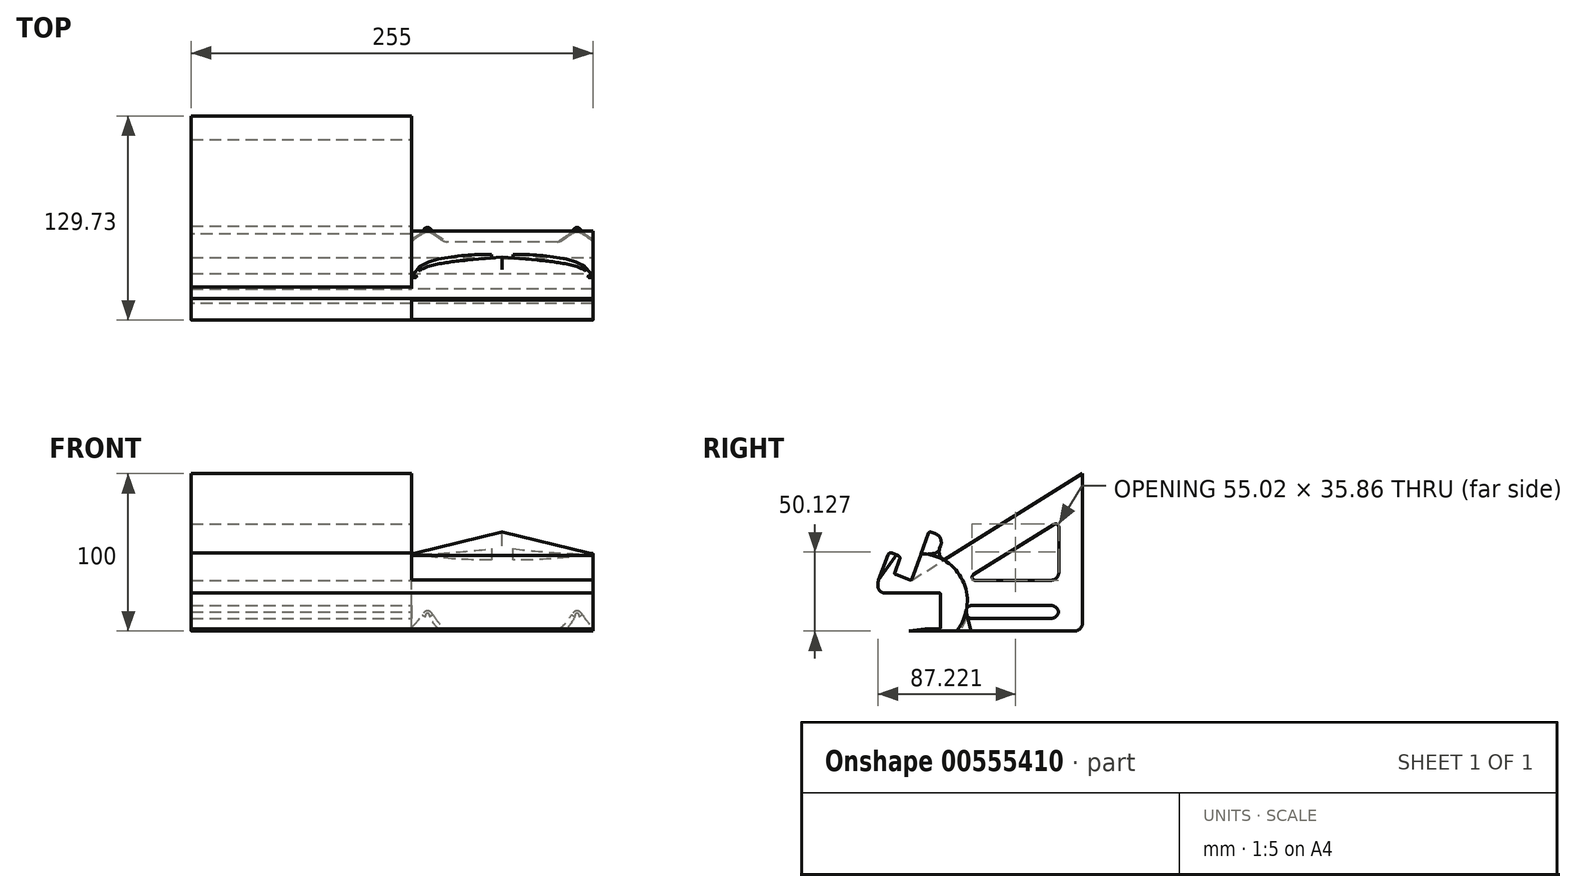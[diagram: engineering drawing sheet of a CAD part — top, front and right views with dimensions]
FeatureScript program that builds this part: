
annotation { "Feature Type Name" : "Feature", "Feature Type Description" : "" }
export const myFeature = defineFeature(function(context is Context, id is Id, definition is map)
    precondition{}
    {
        {
            var Q0;
            Q0=qCreatedBy(makeId("Right.planeOp"),FACE);
            var sketch = newSketch(context, id + "F0", { "sketchPlane" : qUnion([Q0])});
            skLineSegment(sketch, "E0", {"start": v(0, 0) * mm, "end": v(0, 100) * mm});
            skLineSegment(sketch, "E1", {"start": v(0, 0) * mm, "end": v(-110, 0) * mm});
            skLineSegment(sketch, "E2", {"start": v(-110, 0) * mm, "end": v(-110, 1.2) * mm});
            skLineSegment(sketch, "E3", {"start": v(-110, 1.2) * mm, "end": v(-90, 1.2) * mm});
            skLineSegment(sketch, "E4", {"start": v(-90, 1.2) * mm, "end": v(-90, 24.2) * mm});
            skLineSegment(sketch, "E5", {"start": v(-90, 24.2) * mm, "end": v(-110, 24.2) * mm});
            skLineSegment(sketch, "E6", {"start": v(-110, 24.2) * mm, "end": v(-129.73, 31.38) * mm});
            skLineSegment(sketch, "E7", {"start": v(-129.73, 31.38) * mm, "end": v(-122.9, 50.18) * mm});
            skLineSegment(sketch, "E8.0", {"start": v(-119.48, 36.16) * mm, "end": v(-115.38, 47.44) * mm});
            skLineSegment(sketch, "E8.1", {"start": v(-108.59, 32.2) * mm, "end": v(-119.48, 36.16) * mm});
            skLineSegment(sketch, "E9", {"start": v(-122.9, 50.18) * mm, "end": v(-115.38, 47.44) * mm});
            skLineSegment(sketch, "E10", {"start": v(-108.59, 32.2) * mm, "end": v(-108.59, 24.2) * mm, "construction": true});
            skLineSegment(sketch, "E11", {"start": v(-108.59, 32.2) * mm, "end": v(0, 100) * mm});
            skLineSegment(sketch, "E12", {"start": v(-129.73, 31.38) * mm, "end": v(-129.73, 24.2) * mm});
            skLineSegment(sketch, "E13", {"start": v(-129.73, 24.2) * mm, "end": v(-110, 24.2) * mm});
            skLineSegment(sketch, "E14", {"start": v(-75, 24.2) * mm, "end": v(-15, 24.2) * mm});
            skLineSegment(sketch, "E15", {"start": v(-75, 24.2) * mm, "end": v(-75, 32.2) * mm});
            skLineSegment(sketch, "E16", {"start": v(-75, 32.2) * mm, "end": v(-15, 69.66) * mm});
            skLineSegment(sketch, "E17", {"start": v(-15, 24.2) * mm, "end": v(-15, 69.66) * mm});
            skLineSegment(sketch, "E18", {"start": v(-75, 32.2) * mm, "end": v(-15, 32.2) * mm});
            skLineSegment(sketch, "E19", {"start": v(-15, 16.2) * mm, "end": v(-15, 8) * mm});
            skLineSegment(sketch, "E20", {"start": v(-15, 16.2) * mm, "end": v(-75, 16.2) * mm});
            skLineSegment(sketch, "E21", {"start": v(-75, 16.2) * mm, "end": v(-75, 8) * mm});
            skLineSegment(sketch, "E22", {"start": v(-75, 8) * mm, "end": v(-15, 8) * mm});
            skLineSegment(sketch, "E23", {"start": v(-90, 0) * mm, "end": v(-80, 0) * mm, "construction": true});
            skSolve(sketch);
        }
        {
            var Q0;
            Q0=makeQuery(id+"F0.imprint","IMPRINT",FACE,{"disambiguationData":[TD([[makeQuery(id+"F0.imprint","IMPRINT",EDGE,{"derivedFrom":sQuery(id+"F0.wireOp",EDGE,"E0")}),1.0]])]});
            var Q1;
            {var subQ0=sQuery(id+"F0.wireOp",EDGE,"E14");Q1=makeQuery(id+"F0.imprint","IMPRINT",FACE,{"disambiguationData":[TD([[makeQuery(id+"F0.imprint","IMPRINT",EDGE,{"derivedFrom":subQ0}),1.0]])]});}
            var Q2;
            Q2=makeQuery(id+"F0.imprint","IMPRINT",FACE,{"disambiguationData":[TD([[makeQuery(id+"F0.imprint","IMPRINT",EDGE,{"derivedFrom":sQuery(id+"F0.wireOp",EDGE,"E6")}),1.0]])]});
            extrude(context, id + "F1", {"entities" : qUnion([Q0, Q1, Q2]), "oppositeDirection" : true, "depth" : 140 * mm, "offsetDistance" : 25 * mm});
        }
        {
            var Q0;
            Q0=qCreatedBy(makeId("Right.planeOp"),FACE);
            var sketch = newSketch(context, id + "F2", { "sketchPlane" : qUnion([Q0])});
            skLineSegment(sketch, "E24.0", {"start": v(-122.9, 50.18) * mm, "end": v(-115.38, 47.44) * mm});
            skLineSegment(sketch, "E24.1", {"start": v(-129.73, 31.38) * mm, "end": v(-122.9, 50.18) * mm});
            skLineSegment(sketch, "E24.2", {"start": v(-119.48, 36.16) * mm, "end": v(-115.38, 47.44) * mm});
            skLineSegment(sketch, "E24.3", {"start": v(-108.59, 32.2) * mm, "end": v(-119.48, 36.16) * mm});
            skLineSegment(sketch, "E24.4", {"start": v(-110, 24.2) * mm, "end": v(-129.73, 31.38) * mm});
            skLineSegment(sketch, "E24.5", {"start": v(-129.73, 24.2) * mm, "end": v(-110, 24.2) * mm});
            skLineSegment(sketch, "E24.6", {"start": v(-129.73, 31.38) * mm, "end": v(-129.73, 24.2) * mm});
            skLineSegment(sketch, "E24.7", {"start": v(-90, 24.2) * mm, "end": v(-110, 24.2) * mm});
            skLineSegment(sketch, "E24.8", {"start": v(-90, 1.2) * mm, "end": v(-90, 24.2) * mm});
            skLineSegment(sketch, "E24.9", {"start": v(-110, 1.2) * mm, "end": v(-90, 1.2) * mm});
            skLineSegment(sketch, "E24.10", {"start": v(0, 0) * mm, "end": v(-110, 0) * mm});
            skLineSegment(sketch, "E24.11", {"start": v(-110, 0) * mm, "end": v(-110, 1.2) * mm});
            skLineSegment(sketch, "E25", {"start": v(-90, 0) * mm, "end": v(-80, 0) * mm, "construction": true});
            skArc(sketch, "E26", {"start": v(-80, 0) * mm, "mid": v(-85.1, 24.26) * mm, "end": v(-108.59, 32.2) * mm});
            skLineSegment(sketch, "E27", {"start": v(-108.59, 32.2) * mm, "end": v(-102.41, 49.17) * mm});
            skLineSegment(sketch, "E28", {"start": v(-108.59, 32.2) * mm, "end": v(-80, 0) * mm, "construction": true});
            skLineSegment(sketch, "E29", {"start": v(-94.3, 16.1) * mm, "end": v(-85.1, 24.26) * mm, "construction": true});
            skArc(sketch, "E30", {"start": v(-80, 0) * mm, "mid": v(-75.77, 31.62) * mm, "end": v(-102.41, 49.17) * mm});
            skLineSegment(sketch, "E31", {"start": v(-103.07, 19.18) * mm, "end": v(-90, 24.2) * mm, "construction": true});
            skLineSegment(sketch, "E32", {"start": v(-94.3, 16.1) * mm, "end": v(-76.08, 32.27) * mm, "construction": true});
            skSolve(sketch);
        }
        {
            var Q0;
            Q0=makeQuery(id+"F2.imprint","IMPRINT",FACE,{"disambiguationData":[TD([[makeQuery(id+"F2.imprint","IMPRINT",EDGE,{"derivedFrom":sQuery(id+"F2.wireOp",EDGE,"E24.4")}),1.0]])]});
            var Q1;
            Q1=makeQuery(id+"F2.imprint","IMPRINT",FACE,{"disambiguationData":[TD([[makeQuery(id+"F2.imprint","IMPRINT",EDGE,{"derivedFrom":sQuery(id+"F2.wireOp",EDGE,"E24.0")}),-1.0]])]});
            var Q2;
            Q2=makeQuery(id+"F2.imprint","IMPRINT",FACE,{"disambiguationData":[TD([[makeQuery(id+"F2.imprint","IMPRINT",EDGE,{"derivedFrom":sQuery(id+"F2.wireOp",EDGE,"E26")}),-1.0]])]});
            extrude(context, id + "F3", {"entities" : qUnion([Q0, Q1, Q2]), "depth" : 115 * mm, "offsetDistance" : 25 * mm});
        }
        {
            var Q0;
            Q0=makeQuery(id+"F1.opExtrude","SWEPT_EDGE",EDGE,{"disambiguationData":[OSD([sQuery(id+"F0.wireOp",EDGE,"E8.0"),sQuery(id+"F0.wireOp",EDGE,"E8.1")])]});
            var Q1;
            Q1=makeQuery(id+"F3.opExtrude","SWEPT_EDGE",EDGE,{"disambiguationData":[OSD([sQuery(id+"F2.wireOp",EDGE,"E24.2"),sQuery(id+"F2.wireOp",EDGE,"E24.3")])]});
            var Q2;
            Q2=makeQuery(id+"F3.opExtrude","SWEPT_EDGE",EDGE,{"disambiguationData":[OSD([sQuery(id+"F2.wireOp",EDGE,"E24.3"),sQuery(id+"F2.wireOp",EDGE,"E26"),sQuery(id+"F2.wireOp",EDGE,"E27")])]});
            fillet(context, id + "F4", {"entities" : qUnion([Q0, Q1, Q2]), "radius" : 1 * mm, "tangentPropagation" : true, "allowEdgeOverflow" : false});
        }
        {
            var Q0;
            Q0=makeQuery(id+"F1.opExtrude","SWEPT_EDGE",EDGE,{"disambiguationData":[OSD([sQuery(id+"F0.wireOp",EDGE,"E6"),sQuery(id+"F0.wireOp",EDGE,"E7"),sQuery(id+"F0.wireOp",EDGE,"E12")])]});
            var Q1;
            Q1=makeQuery(id+"F3.opExtrude","SWEPT_EDGE",EDGE,{"disambiguationData":[OSD([sQuery(id+"F2.wireOp",EDGE,"E24.1"),sQuery(id+"F2.wireOp",EDGE,"E24.4"),sQuery(id+"F2.wireOp",EDGE,"E24.6")])]});
            fillet(context, id + "F5", {"entities" : qUnion([Q0, Q1]), "radius" : 5 * mm, "tangentPropagation" : true, "allowEdgeOverflow" : false});
        }
        {
            var Q0;
            Q0=makeQuery(id+"F1.opExtrude","SWEPT_EDGE",EDGE,{"disambiguationData":[OSD([sQuery(id+"F0.wireOp",EDGE,"E2"),sQuery(id+"F0.wireOp",EDGE,"E3")])]});
            var Q1;
            Q1=makeQuery(id+"F1.opExtrude","SWEPT_EDGE",EDGE,{"disambiguationData":[OSD([sQuery(id+"F0.wireOp",EDGE,"E12"),sQuery(id+"F0.wireOp",EDGE,"E13")])]});
            var Q2;
            Q2=makeQuery(id+"F3.opExtrude","SWEPT_EDGE",EDGE,{"disambiguationData":[OSD([sQuery(id+"F2.wireOp",EDGE,"E24.5"),sQuery(id+"F2.wireOp",EDGE,"E24.6")])]});
            fillet(context, id + "F6", {"entities" : qUnion([Q0, Q1, Q2]), "radius" : 4 * mm, "tangentPropagation" : true, "allowEdgeOverflow" : false});
        }
        {
            var Q0;
            Q0=makeQuery(id+"F1.opExtrude","SWEPT_EDGE",EDGE,{"disambiguationData":[OSD([sQuery(id+"F0.wireOp",EDGE,"E21"),sQuery(id+"F0.wireOp",EDGE,"E22")])]});
            var Q1;
            Q1=makeQuery(id+"F1.opExtrude","SWEPT_EDGE",EDGE,{"disambiguationData":[OSD([sQuery(id+"F0.wireOp",EDGE,"E20"),sQuery(id+"F0.wireOp",EDGE,"E21")])]});
            var Q2;
            Q2=makeQuery(id+"F1.opExtrude","SWEPT_EDGE",EDGE,{"disambiguationData":[OSD([sQuery(id+"F0.wireOp",EDGE,"E19"),sQuery(id+"F0.wireOp",EDGE,"E20")])]});
            var Q3;
            Q3=makeQuery(id+"F1.opExtrude","SWEPT_EDGE",EDGE,{"disambiguationData":[OSD([sQuery(id+"F0.wireOp",EDGE,"E19"),sQuery(id+"F0.wireOp",EDGE,"E22")])]});
            var Q4;
            Q4=makeQuery(id+"F1.opExtrude","SWEPT_EDGE",EDGE,{"disambiguationData":[OSD([sQuery(id+"F0.wireOp",EDGE,"E17"),sQuery(id+"F0.wireOp",EDGE,"E18")])]});
            fillet(context, id + "F7", {"entities" : qUnion([Q0, Q1, Q2, Q3, Q4]), "radius" : 5 * mm, "tangentPropagation" : true, "allowEdgeOverflow" : false});
        }
        {
            var Q0;
            Q0=makeQuery(id+"F1.opExtrude","SWEPT_EDGE",EDGE,{"disambiguationData":[OSD([sQuery(id+"F0.wireOp",EDGE,"E15"),sQuery(id+"F0.wireOp",EDGE,"E16"),sQuery(id+"F0.wireOp",EDGE,"E18")])]});
            var Q1;
            Q1=makeQuery(id+"F1.opExtrude","SWEPT_EDGE",EDGE,{"disambiguationData":[OSD([sQuery(id+"F0.wireOp",EDGE,"E16"),sQuery(id+"F0.wireOp",EDGE,"E17")])]});
            fillet(context, id + "F8", {"entities" : qUnion([Q0, Q1]), "radius" : 2 * mm, "tangentPropagation" : true, "allowEdgeOverflow" : false});
        }
        {
            var Q0;
            Q0=makeQuery(id+"F3.opExtrude","SWEPT_EDGE",EDGE,{"disambiguationData":[OSD([sQuery(id+"F2.wireOp",EDGE,"E24.0"),sQuery(id+"F2.wireOp",EDGE,"E24.1")])]});
            chamfer(context, id + "F9", {"entities" : qUnion([Q0]), "chamferType" : ChamferType.TWO_OFFSETS, "width1" : 19 * mm, "oppositeDirection" : false, "width2" : 5 * mm, "tangentPropagation" : true});
        }
        {
            var Q0;
            Q0=makeQuery(id+"F1.opExtrude","SWEPT_EDGE",EDGE,{"disambiguationData":[OSD([sQuery(id+"F0.wireOp",EDGE,"E7"),sQuery(id+"F0.wireOp",EDGE,"E9")])]});
            var Q1;
            Q1=makeQuery(id+"F1.opExtrude","SWEPT_EDGE",EDGE,{"disambiguationData":[OSD([sQuery(id+"F0.wireOp",EDGE,"E8.0"),sQuery(id+"F0.wireOp",EDGE,"E9")])]});
            var Q2;
            Q2=makeQuery(id+"F3.opExtrude","SWEPT_EDGE",EDGE,{"disambiguationData":[OSD([sQuery(id+"F2.wireOp",EDGE,"E24.0"),sQuery(id+"F2.wireOp",EDGE,"E24.2")])]});
            var Q3;
            Q3=makeQuery(id+"F3.opExtrude","SWEPT_EDGE",EDGE,{"disambiguationData":[OSD([sQuery(id+"F2.wireOp",EDGE,"E24.0"),sQuery(id+"F2.wireOp",EDGE,"E24.1")])]});
            var Q4;
            {var subQ0=sQuery(id+"F2.wireOp",EDGE,"E24.0");Q4=makeQuery(id+"F9.opChamfer","BLEND_EDGE",EDGE,{"blendedFrom":[makeQuery(id+"F3.opExtrude","SWEPT_EDGE",EDGE,{"disambiguationData":[OSD([subQ0,sQuery(id+"F2.wireOp",EDGE,"E24.1")])]}),makeQuery(id+"F3.opExtrude","SWEPT_FACE",FACE,{"disambiguationData":[OSD([subQ0])]})],"blendedInto":[makeQuery(id+"F3.opExtrude","SWEPT_FACE",FACE,{"disambiguationData":[OSD([subQ0])]})]});}
            fillet(context, id + "F10", {"entities" : qUnion([Q0, Q1, Q2, Q3, Q4]), "radius" : 2 * mm, "tangentPropagation" : true, "allowEdgeOverflow" : false});
        }
        {
            var Q0;
            Q0=makeQuery(id+"F1.opExtrude","SWEPT_EDGE",EDGE,{"disambiguationData":[OSD([sQuery(id+"F0.wireOp",EDGE,"E3"),sQuery(id+"F0.wireOp",EDGE,"E4")])]});
            var Q1;
            Q1=makeQuery(id+"F1.opExtrude","SWEPT_EDGE",EDGE,{"disambiguationData":[OSD([sQuery(id+"F0.wireOp",EDGE,"E4"),sQuery(id+"F0.wireOp",EDGE,"E5")])]});
            var Q2;
            Q2=makeQuery(id+"F3.opExtrude","SWEPT_EDGE",EDGE,{"disambiguationData":[OSD([sQuery(id+"F2.wireOp",EDGE,"E24.8"),sQuery(id+"F2.wireOp",EDGE,"E24.9")])]});
            var Q3;
            Q3=makeQuery(id+"F3.opExtrude","SWEPT_EDGE",EDGE,{"disambiguationData":[OSD([sQuery(id+"F2.wireOp",EDGE,"E24.7"),sQuery(id+"F2.wireOp",EDGE,"E24.8")])]});
            fillet(context, id + "F11", {"entities" : qUnion([Q0, Q1, Q2, Q3]), "radius" : 1 * mm, "tangentPropagation" : true, "allowEdgeOverflow" : false});
        }
        {
            var Q0;
            Q0=makeQuery(id+"F1.opExtrude","SWEPT_EDGE",EDGE,{"disambiguationData":[OSD([sQuery(id+"F0.wireOp",EDGE,"E0"),sQuery(id+"F0.wireOp",EDGE,"E1")])]});
            fillet(context, id + "F12", {"entities" : qUnion([Q0]), "radius" : 5 * mm, "tangentPropagation" : true, "allowEdgeOverflow" : false});
        }
        {
            var Q0;
            Q0=makeQuery(id+"F3.opExtrude","SWEPT_FACE",FACE,{"disambiguationData":[OSD([sQuery(id+"F2.wireOp",EDGE,"E27")])]});
            var sketch = newSketch(context, id + "F13", { "sketchPlane" : qUnion([Q0])});
            skLineSegment(sketch, "E33.0", {"start": v(0, -6.88) * mm, "end": v(0, 11.18) * mm});
            skLineSegment(sketch, "E33.1", {"start": v(115, 11.18) * mm, "end": v(0, 11.18) * mm});
            skLineSegment(sketch, "E33.2", {"start": v(115, -18.42) * mm, "end": v(115, 11.18) * mm});
            skLineSegment(sketch, "E34", {"start": v(57.5, 11.18) * mm, "end": v(57.5, 26.18) * mm, "construction": true});
            skPoint(sketch, "E34.endSnap0", {"position": v(57.5, 11.18) * mm});
            skLineSegment(sketch, "E35", {"start": v(0, 11.18) * mm, "end": v(57.5, 26.18) * mm});
            skLineSegment(sketch, "E36", {"start": v(57.5, 26.18) * mm, "end": v(115, 11.18) * mm});
            skSolve(sketch);
        }
        {
            var Q0;
            Q0=makeQuery(id+"F13.imprint","IMPRINT",FACE,{"disambiguationData":[TD([[makeQuery(id+"F13.imprint","IMPRINT",EDGE,{"derivedFrom":sQuery(id+"F13.wireOp",EDGE,"E33.1")}),-1.0]])]});
            extrude(context, id + "F14", {"entities" : qUnion([Q0]), "operationType" : NewBodyOperationType.ADD, "oppositeDirection" : true, "depth" : 10 * mm, "offsetDistance" : 25 * mm});
        }
        {
            var Q0;
            Q0=makeQuery(id+"F14.boolean.opBoolean","INTERSECT",EDGE,{"derivedFrom":[makeQuery(id+"F3.opExtrude","SWEPT_FACE",FACE,{"disambiguationData":[OSD([sQuery(id+"F2.wireOp",EDGE,"E30")])]}),makeQuery(id+"F14.opExtrude","CAP_FACE",FACE,{"disambiguationData":[OSD([sQuery(id+"F13.wireOp",EDGE,"E33.1"),sQuery(id+"F13.wireOp",EDGE,"E35"),sQuery(id+"F13.wireOp",EDGE,"E36")])],"isStart":false})]});
            var Q1;
            Q1=makeQuery(id+"F14.boolean.opBoolean","INTERSECT",EDGE,{"derivedFrom":[makeQuery(id+"F3.opExtrude","SWEPT_FACE",FACE,{"disambiguationData":[OSD([sQuery(id+"F2.wireOp",EDGE,"E30")])]}),makeQuery(id+"F14.opExtrude","SWEPT_FACE",FACE,{"disambiguationData":[OSD([sQuery(id+"F13.wireOp",EDGE,"E36")])]})]});
            var Q2;
            Q2=makeQuery(id+"F14.boolean.opBoolean","INTERSECT",EDGE,{"derivedFrom":[makeQuery(id+"F3.opExtrude","SWEPT_FACE",FACE,{"disambiguationData":[OSD([sQuery(id+"F2.wireOp",EDGE,"E30")])]}),makeQuery(id+"F14.opExtrude","SWEPT_FACE",FACE,{"disambiguationData":[OSD([sQuery(id+"F13.wireOp",EDGE,"E35")])]})]});
            var Q3;
            Q3=makeQuery(id+"F14.opExtrude","CAP_EDGE",EDGE,{"disambiguationData":[OSD([sQuery(id+"F13.wireOp",EDGE,"E36")])],"isStart":false});
            var Q4;
            Q4=makeQuery(id+"F14.opExtrude","CAP_EDGE",EDGE,{"disambiguationData":[OSD([sQuery(id+"F13.wireOp",EDGE,"E35")])],"isStart":false});
            fillet(context, id + "F15", {"entities" : qUnion([Q0, Q1, Q2, Q3, Q4]), "radius" : 6 * mm, "tangentPropagation" : true, "allowEdgeOverflow" : false});
        }
        {
            var Q0;
            Q0=makeQuery(id+"F14.opExtrude","CAP_EDGE",EDGE,{"disambiguationData":[OSD([sQuery(id+"F13.wireOp",EDGE,"E35")])],"isStart":true});
            var Q1;
            Q1=makeQuery(id+"F14.opExtrude","CAP_EDGE",EDGE,{"disambiguationData":[OSD([sQuery(id+"F13.wireOp",EDGE,"E36")])],"isStart":true});
            fillet(context, id + "F16", {"entities" : qUnion([Q0, Q1]), "radius" : 1 * mm, "tangentPropagation" : true, "allowEdgeOverflow" : false});
        }
        {
            var Q0;
            Q0=makeQuery(id+"F3.opExtrude","SWEPT_FACE",FACE,{"disambiguationData":[OSD([sQuery(id+"F2.wireOp",EDGE,"E24.10")])]});
            var sketch = newSketch(context, id + "F17", { "sketchPlane" : qUnion([Q0])});
            skLineSegment(sketch, "E37.0", {"start": v(115, 80) * mm, "end": v(0, 80) * mm});
            skLineSegment(sketch, "E38", {"start": v(0, 80) * mm, "end": v(10, 80) * mm, "construction": true});
            skLineSegment(sketch, "E39", {"start": v(10, 80) * mm, "end": v(20, 80) * mm, "construction": true});
            skLineSegment(sketch, "E40", {"start": v(20, 80) * mm, "end": v(10, 70) * mm});
            skLineSegment(sketch, "E41", {"start": v(10, 70) * mm, "end": v(0, 80) * mm});
            skLineSegment(sketch, "E42", {"start": v(57.5, 80) * mm, "end": v(57.5, 89.56) * mm, "construction": true});
            skLineSegment(sketch, "E43.MirrorCS", {"start": v(95, 80) * mm, "end": v(105, 70) * mm});
            skLineSegment(sketch, "E44.MirrorCS", {"start": v(105, 70) * mm, "end": v(115, 80) * mm});
            skLineSegment(sketch, "E45.MirrorCS", {"start": v(115, 80) * mm, "end": v(105, 80) * mm, "construction": true});
            skLineSegment(sketch, "E46.MirrorCS", {"start": v(105, 80) * mm, "end": v(95, 80) * mm, "construction": true});
            skSolve(sketch);
        }
        {
            var Q0;
            Q0 = qSketchRegion(id + "F17", true);
            extrude(context, id + "F18", {"entities" : qUnion([Q0]), "operationType" : NewBodyOperationType.ADD, "oppositeDirection" : true, "depth" : 25 * mm, "offsetDistance" : 25 * mm, "hasDraft" : true, "draftAngle" : 10 * degree, "draftPullDirection" : true});
        }
        {
            var Q0;
            Q0=makeQuery(id+"F18.opExtrude","SWEPT_EDGE",EDGE,{"disambiguationData":[OSD([sQuery(id+"F17.wireOp",EDGE,"E43.MirrorCS"),sQuery(id+"F17.wireOp",EDGE,"E44.MirrorCS")])]});
            var Q1;
            Q1=makeQuery(id+"F18.opExtrude","SWEPT_EDGE",EDGE,{"disambiguationData":[OSD([sQuery(id+"F17.wireOp",EDGE,"E40"),sQuery(id+"F17.wireOp",EDGE,"E41")])]});
            fillet(context, id + "F19", {"entities" : qUnion([Q0, Q1]), "radius" : 2 * mm, "tangentPropagation" : true, "allowEdgeOverflow" : false});
        }
        {
            var Q0;
            Q0=makeQuery(id+"F18.boolean.opBoolean","INTERSECT",EDGE,{"derivedFrom":[makeQuery(id+"F3.opExtrude","SWEPT_FACE",FACE,{"disambiguationData":[OSD([sQuery(id+"F2.wireOp",EDGE,"E30")])]}),makeQuery(id+"F18.opExtrude","SWEPT_FACE",FACE,{"disambiguationData":[OSD([sQuery(id+"F17.wireOp",EDGE,"E44.MirrorCS")])]})]});
            var Q1;
            Q1=makeQuery(id+"F18.boolean.opBoolean","INTERSECT",EDGE,{"derivedFrom":[makeQuery(id+"F3.opExtrude","SWEPT_FACE",FACE,{"disambiguationData":[OSD([sQuery(id+"F2.wireOp",EDGE,"E30")])]}),makeQuery(id+"F18.opExtrude","SWEPT_FACE",FACE,{"disambiguationData":[OSD([sQuery(id+"F17.wireOp",EDGE,"E40")])]})]});
            fillet(context, id + "F20", {"entities" : qUnion([Q0, Q1]), "radius" : 3 * mm, "tangentPropagation" : true, "allowEdgeOverflow" : false});
        }
        {
            var Q0;
            Q0=makeQuery(id+"F3.opExtrude","SWEPT_EDGE",EDGE,{"disambiguationData":[OSD([sQuery(id+"F2.wireOp",EDGE,"E24.9"),sQuery(id+"F2.wireOp",EDGE,"E24.11")])]});
            chamfer(context, id + "F21", {"entities" : qUnion([Q0]), "chamferType" : ChamferType.TWO_OFFSETS, "width1" : 1 * mm, "oppositeDirection" : false, "width2" : 10 * mm, "tangentPropagation" : true});
        }
    });
